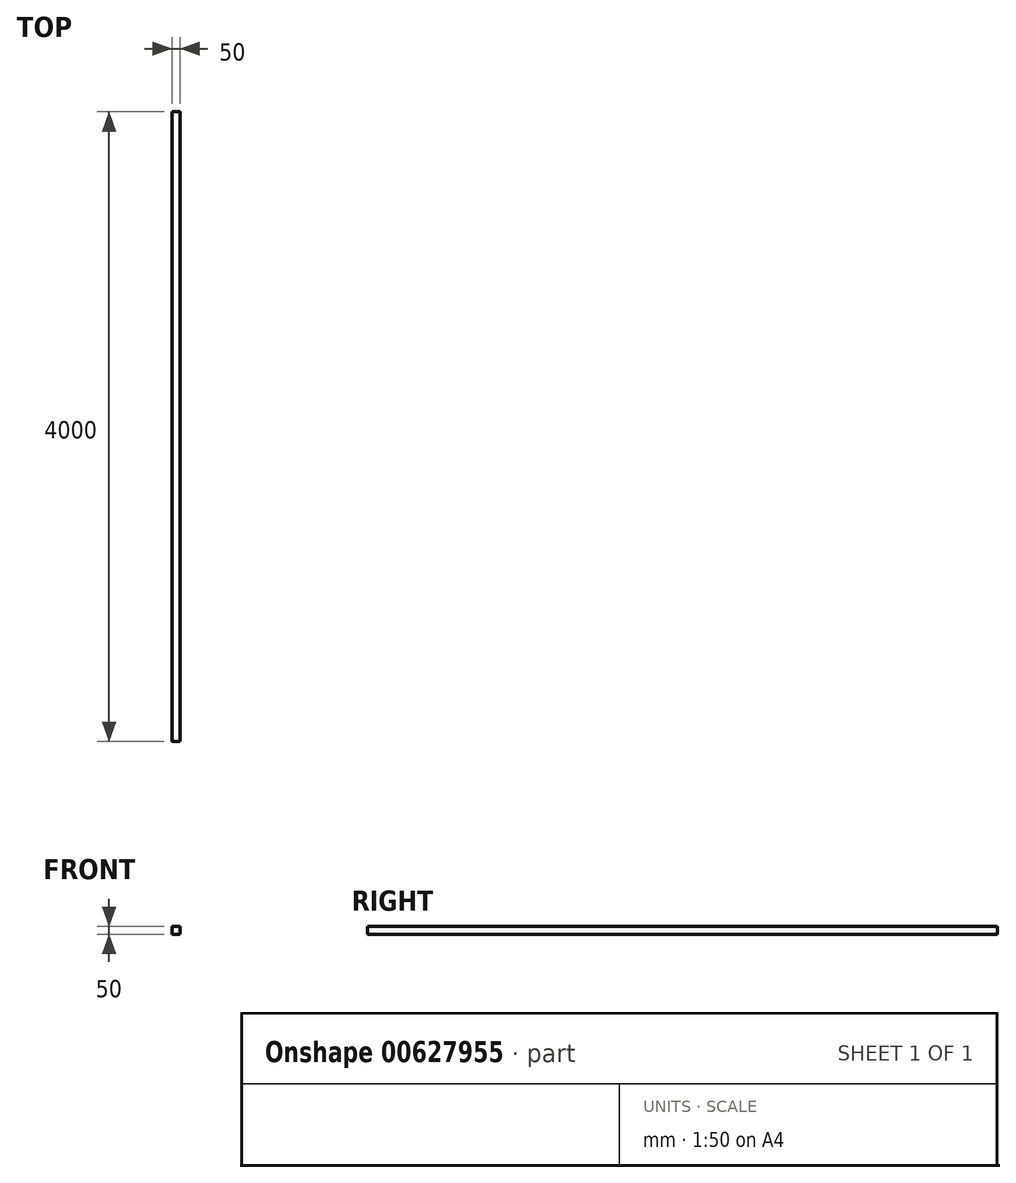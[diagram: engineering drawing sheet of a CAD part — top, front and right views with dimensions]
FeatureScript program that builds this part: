
annotation { "Feature Type Name" : "Feature", "Feature Type Description" : "" }
export const myFeature = defineFeature(function(context is Context, id is Id, definition is map)
    precondition{}
    {
        {
            var Q0;
            Q0=qCreatedBy(makeId("Front.planeOp"),FACE);
            var sketch = newSketch(context, id + "F0", { "sketchPlane" : qUnion([Q0])});
            skLineSegment(sketch, "E0.bottom", {"start": v(0.67, -18.87) * mm, "end": v(44.67, -18.87) * mm});
            skLineSegment(sketch, "E0.top", {"start": v(0.67, 31.13) * mm, "end": v(44.67, 31.13) * mm});
            skLineSegment(sketch, "E0.left", {"start": v(-2.33, -15.87) * mm, "end": v(-2.33, 28.13) * mm});
            skLineSegment(sketch, "E0.right", {"start": v(47.67, -15.87) * mm, "end": v(47.67, 28.13) * mm});
            skPoint(sketch, "E1.visualSharp", {"position": v(-2.33, 31.13) * mm});
            skArc(sketch, "E1.filletArc", {"start": v(0.67, 31.13) * mm, "mid": v(-1.46, 30.26) * mm, "end": v(-2.33, 28.13) * mm});
            skPoint(sketch, "E2.visualSharp", {"position": v(47.67, 31.13) * mm});
            skArc(sketch, "E2.filletArc", {"start": v(47.67, 28.13) * mm, "mid": v(46.79, 30.26) * mm, "end": v(44.67, 31.13) * mm});
            skPoint(sketch, "E3.visualSharp", {"position": v(47.67, -18.87) * mm});
            skArc(sketch, "E3.filletArc", {"start": v(44.67, -18.87) * mm, "mid": v(46.79, -17.99) * mm, "end": v(47.67, -15.87) * mm});
            skPoint(sketch, "E4.visualSharp", {"position": v(-2.33, -18.87) * mm});
            skArc(sketch, "E4.filletArc", {"start": v(-2.33, -15.87) * mm, "mid": v(-1.46, -17.99) * mm, "end": v(0.67, -18.87) * mm});
            skSolve(sketch);
        }
        {
            var Q0;
            Q0=qSketchRegion(id+"F0",true);
            extrude(context, id + "F1", {"entities" : qUnion([Q0]), "depth" : 4000 * mm, "offsetDistance" : 25 * mm});
        }
    });
